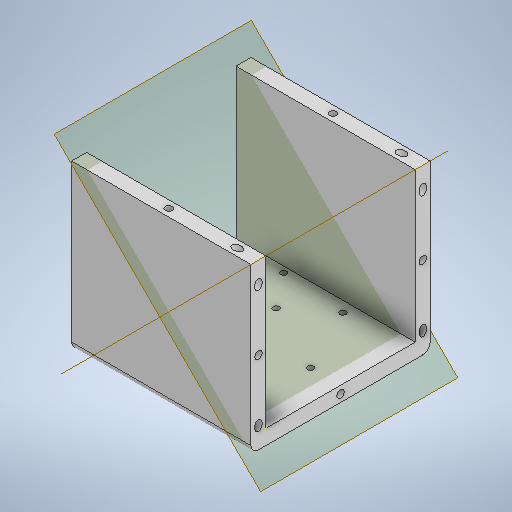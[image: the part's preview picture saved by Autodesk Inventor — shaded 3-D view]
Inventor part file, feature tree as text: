
AUTODESK INVENTOR PART (.ipt)
format: ipt  version: 2025.1 (Build 291241020, 241B)  size: 355,328 bytes
history: native  units: in
note: dims shown in document units (in); Inventor stores cm internally (conversion verified against a paired STEP export)
features: sketch x13, extrude x10, plane x2, fillet x1
ambient origin geometry x8: Origin, YZ Plane, XZ Plane, XY Plane, X Axis, Y Axis, Z Axis, Center Point
bodies: Solid1 (feature_tree)
feature tree (26):
  sketch  "Sketch1"  dims[d0=6.0in d1=6.0in]
  extrude  "Extrusion1"  Depth=6.0in
  extrude  "Extrusion2"  Depth=0.5in
  fillet  "Fillet1"  Radius=0.5in
  extrude  "Extrusion3"  Depth=0.25in
  sketch  "Sketch5"  dims[d16=0.2362in d17=0.2362in]
  extrude  "Extrusion5"  Depth=6.0in
  extrude  "Extrusion6"  Depth=0.2362in
  plane  "Work Plane1"
  extrude  "Extrusion7"  Depth=2.75in
  plane  "Work Plane2"
  extrude  "Extrusion8"  TaperAngle=135.0deg  [1 undecoded]
  extrude  "Extrusion9"  Depth=0.5in TaperAngle=0.0deg
  extrude  "Extrusion10"  Depth=0.5in
  sketch  "Sketch12"  dims[d36=1.0in]
  extrude  "Extrusion11"  Depth=0.5in TaperAngle=0.0deg
  sketch  "Sketch14"  dims[d39=0.205in d40=1.9375in d41=2.041in d42=2.041in d43=0.205in d44=0.157in d45=0.0in d46=1.6in d47=0.205in d48=1.05in d49=1.05in d52=0.157in d53=0.0in d59=0.205in d60=0.205in d61=0.205in d62=1.4in d63=0.5in d64=1.0in d65=0.205in d66=0.205in d67=0.205in d68=0.157in d69=0.0in d9=0.0344in]
  sketch  "Sketch2"  dims[d2=0.5in d3=0.0in d4=0.5in d5=0.5in]
  sketch  "Sketch3"  dims[d6=5.0in d7=0.0in d8=0.25in]
  sketch  "Sketch4"  dims[d11=0.5in d12=0.0in d15=6.0in]
  sketch  "Sketch6"  dims[d18=0.1575in d19=0.0in d20=2.75in]
  sketch  "Sketch7"  dims[d21=0.5in d22=0.0in d23=135.0deg]
  sketch  "Sketch8"  dims[d24=0.5in d25=1.25in d26=1.0in d27=0.0in d28=0.0in]
  sketch  "Sketch10"  dims[d29=90.0deg d30=0.5in]
  sketch  "Sketch11"  dims[d31=0.5in d32=1.0in d33=1.25in d34=0.0in d35=0.0in]
  sketch  "Sketch13"  dims[d37=0.205in]
note: 1 required parameter value undecoded (feature->parameter linkage not recoverable at this tier; creation-order binding heuristic only, values carry confidence <= 0.55)
